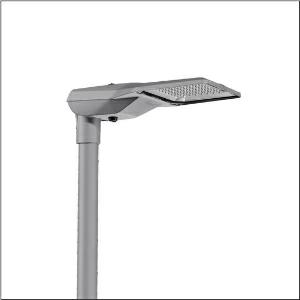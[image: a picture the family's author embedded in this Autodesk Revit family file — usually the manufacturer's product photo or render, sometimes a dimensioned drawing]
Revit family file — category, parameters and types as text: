
# Revit family: streetlight_sl_21_midi___stw1_0a_5xe3e43t08nb_27ab
name_source: partatom
category: Lighting Fixtures
units: mm (PartAtom-declared; Revit-internal decimal feet)

## family parameters
Cut with Voids When Loaded = No
Host = Face
Light Source = No
Part Type = Normal
Room Calculation Point = No
Round Connector Dimension = Use Diameter
Shared = No

## types (1)
- --- (1 x LED, 23710 lm, 151.2 W, 4000K)
    Apparent Load = 151 VA
    CIE Flux Codes = 39 75 98 100 100
    Color Rendering = 70
    Color Temperature = 4000K
    Default Elevation = 1800 mm
    Description = Streetlight SL 21 midi, mast luminaire, primary light control with lens, of PMMA, primary optical cover: cover, of toughened safety glass, transparent, light distribution: STW1.0a, light emission: direct distribution, primary light characteristic: asymmetric, installation type: side-entry, post-top, LED, High Power LED, rated luminous flux: 23.710lm, luminous efficacy: 157lm/W, light colour: 740, colour temperature: 4000K, control: overheat protection, constant luminous flux control, time-dependent luminous flux control, flexible luminous flux parameterisation, presetting dimming logarithmic, mains connection: 230..240V, AC, 50/60Hz, start of lifetime: 151W, end of service life: 157W, reduction: 70W, luminaire housing, of diecast aluminium, powder-coated, Siteco® metallic grey (DB 702S), corrosivity category C5 mid according to DIN EN ISO 12944, please order mast flange separately, inclination adjustable: 0°, 5°, 10°, 15°, sealing non-destructively replaceable, multi-level sealing system, length: 644mm, width: 335mm, height: 110mm, mast flange for spigot size: 42mm (side-entry): 5XC10008XM4, 60/48mm (side-entry/post-top): 5XC10108XM2, 76/60mm (side-entry/post-top): 5XC10108XM1, Smart Interface below and above, protection rating (complete): IP66, insulation class (complete): insulation class II (safety insulation), certification: CE, ENEC, ENEC+, VDE, impact resistance: IK09, permissible operating ambient temperature for outdoor applications: -40..+50°C, standard-compliant lighting for roads and squares, packaging unit: 1 piece

Light Distribution: STW1.0a
    Height = 111 mm
    Lamp = 1 x LED
    Lamp Light Flux = 23710 lm
    Lamp Power = 151.2 W
    Lamp count = 1
    Length = 644 mm
    Luminous efficacy = 157 lm/W
    Manufacturer = Siteco
    ModVariant = No
    Model = 5XE3E43T08NB
    Number of Poles = 1
    OnlyDefault = Yes
    Power Factor = 1
    Product Name = Streetlight SL 21 midi | STW1.0a
    Product group = mast luminaire | pylon top
    ProductGroupID = 6100
    Protection Class = Protection class II
    Protection Degree = IP 66
    RLX_Detail_Level = 1
    RLX_Emergency_Light_Flux = 0 lm
    RLX_Emergency_Type = 0
    RLX_Emergency_Type_DB = No
    RlxData = <blob elided: 91069 chars, md5=cb5bd286>
    Socket = socket
    Standby Power = 0 W
    System Light Flux = 23710 lm
    System Power = 151 W
    Type Comments = factory setting: luminous flux: 100 % | dim-lin: 254 | 802 mA
    Type Image = l_1004304.jpg
    URL = http://relux.com
    VarID = @adj_102115
    Voltage = 0 V
    Weight = 0.00 kg
    Width = 336 mm

## geometry (parser evidence)
native form markers: Blend x4, Sweep x10
no freeform markers — native parametric forms only
